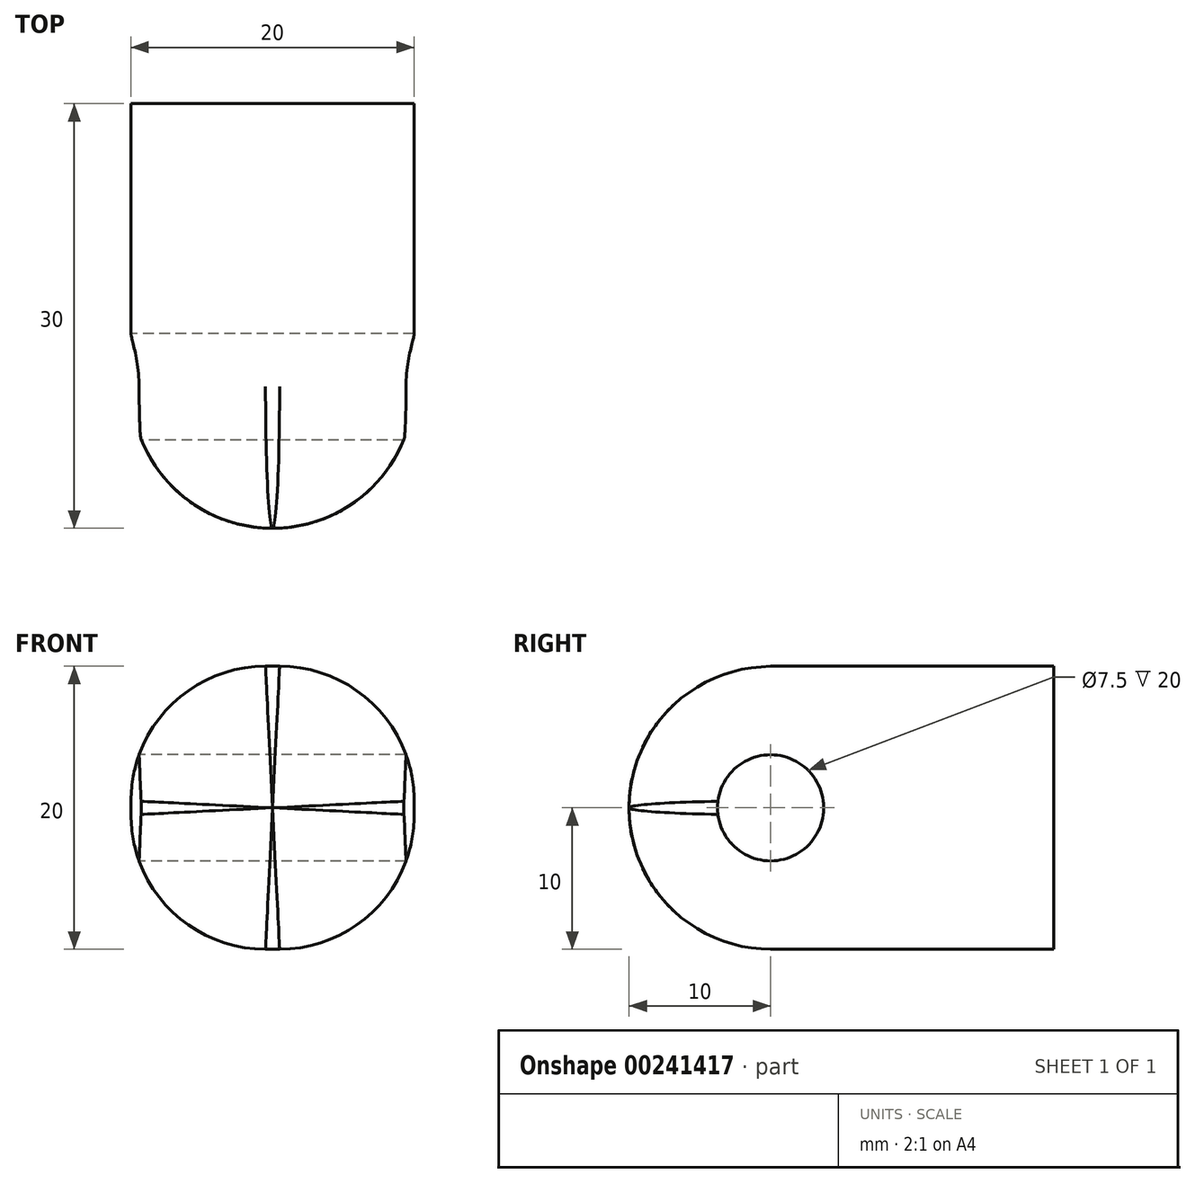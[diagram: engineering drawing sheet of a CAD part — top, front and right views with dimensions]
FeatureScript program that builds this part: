
annotation { "Feature Type Name" : "Feature", "Feature Type Description" : "" }
export const myFeature = defineFeature(function(context is Context, id is Id, definition is map)
    precondition{}
    {
        {
            var Q0;
            Q0=qCreatedBy(makeId("Front.planeOp"),FACE);
            var sketch = newSketch(context, id + "F0", { "sketchPlane" : qUnion([Q0])});
            skLineSegment(sketch, "E0.bottom", {"start": v(-10, 10) * mm, "end": v(10, 10) * mm});
            skLineSegment(sketch, "E0.top", {"start": v(-10, -10) * mm, "end": v(10, -10) * mm});
            skLineSegment(sketch, "E0.left", {"start": v(-10, 10) * mm, "end": v(-10, -10) * mm});
            skLineSegment(sketch, "E0.right", {"start": v(10, 10) * mm, "end": v(10, -10) * mm});
            skPoint(sketch, "E0.middle", {"position": v(0, 0) * mm});
            skSolve(sketch);
        }
        {
            var Q0;
            Q0 = qSketchRegion(id + "F0", true);
            extrude(context, id + "F1", {"entities" : qUnion([Q0]), "depth" : 30 * mm});
        }
        {
            var Q0;
            Q0=makeQuery(id+"F1.opExtrude","SWEPT_FACE",FACE,{"disambiguationData":[OSD([sQuery(id+"F0.wireOp",EDGE,"E0.left")])]});
            var sketch = newSketch(context, id + "F2", { "sketchPlane" : qUnion([Q0])});
            skCircle(sketch, "E1", {"center": v(20, 0) * mm, "radius": 3.75 * mm});
            skSolve(sketch);
        }
        {
            var Q0;
            Q0 = qSketchRegion(id + "F2", true);
            extrude(context, id + "F3", {"entities" : qUnion([Q0]), "operationType" : NewBodyOperationType.REMOVE, "endBound" : BoundingType.THROUGH_ALL, "oppositeDirection" : true, "depth" : 25 * mm});
        }
        {
            var Q0;
            Q0=makeQuery(id+"F1.opExtrude","CAP_FACE",FACE,{"disambiguationData":[OSD([sQuery(id+"F0.wireOp",EDGE,"E0.bottom"),sQuery(id+"F0.wireOp",EDGE,"E0.top"),sQuery(id+"F0.wireOp",EDGE,"E0.left"),sQuery(id+"F0.wireOp",EDGE,"E0.right")])],"isStart":false});
            fillet(context, id + "F4", {"entities" : qUnion([Q0]), "radius" : 10 * mm, "tangentPropagation" : true, "allowEdgeOverflow" : false});
        }
        {
            var Q0;
            Q0=makeQuery(id+"F4.opFillet","BLEND_EDGE",EDGE,{"blendedFrom":[makeQuery(id+"F1.opExtrude","CAP_EDGE",EDGE,{"disambiguationData":[OSD([sQuery(id+"F0.wireOp",EDGE,"E0.bottom")])],"isStart":false}),makeQuery(id+"F1.opExtrude","CAP_EDGE",EDGE,{"disambiguationData":[OSD([sQuery(id+"F0.wireOp",EDGE,"E0.right")])],"isStart":false})],"blendedInto":[]});
            var Q1;
            Q1=makeQuery(id+"F4.opFillet","BLEND_EDGE",EDGE,{"blendedFrom":[makeQuery(id+"F1.opExtrude","CAP_EDGE",EDGE,{"disambiguationData":[OSD([sQuery(id+"F0.wireOp",EDGE,"E0.bottom")])],"isStart":false}),makeQuery(id+"F1.opExtrude","CAP_EDGE",EDGE,{"disambiguationData":[OSD([sQuery(id+"F0.wireOp",EDGE,"E0.left")])],"isStart":false})],"blendedInto":[]});
            var Q2;
            Q2=makeQuery(id+"F4.opFillet","BLEND_EDGE",EDGE,{"blendedFrom":[makeQuery(id+"F1.opExtrude","CAP_EDGE",EDGE,{"disambiguationData":[OSD([sQuery(id+"F0.wireOp",EDGE,"E0.top")])],"isStart":false}),makeQuery(id+"F1.opExtrude","CAP_EDGE",EDGE,{"disambiguationData":[OSD([sQuery(id+"F0.wireOp",EDGE,"E0.left")])],"isStart":false})],"blendedInto":[]});
            var Q3;
            Q3=makeQuery(id+"F4.opFillet","BLEND_EDGE",EDGE,{"blendedFrom":[makeQuery(id+"F1.opExtrude","CAP_EDGE",EDGE,{"disambiguationData":[OSD([sQuery(id+"F0.wireOp",EDGE,"E0.top")])],"isStart":false}),makeQuery(id+"F1.opExtrude","CAP_EDGE",EDGE,{"disambiguationData":[OSD([sQuery(id+"F0.wireOp",EDGE,"E0.right")])],"isStart":false})],"blendedInto":[]});
            fillet(context, id + "F5", {"entities" : qUnion([Q0, Q1, Q2, Q3]), "radius" : 9.5 * mm, "tangentPropagation" : true, "allowEdgeOverflow" : false});
        }
    });
